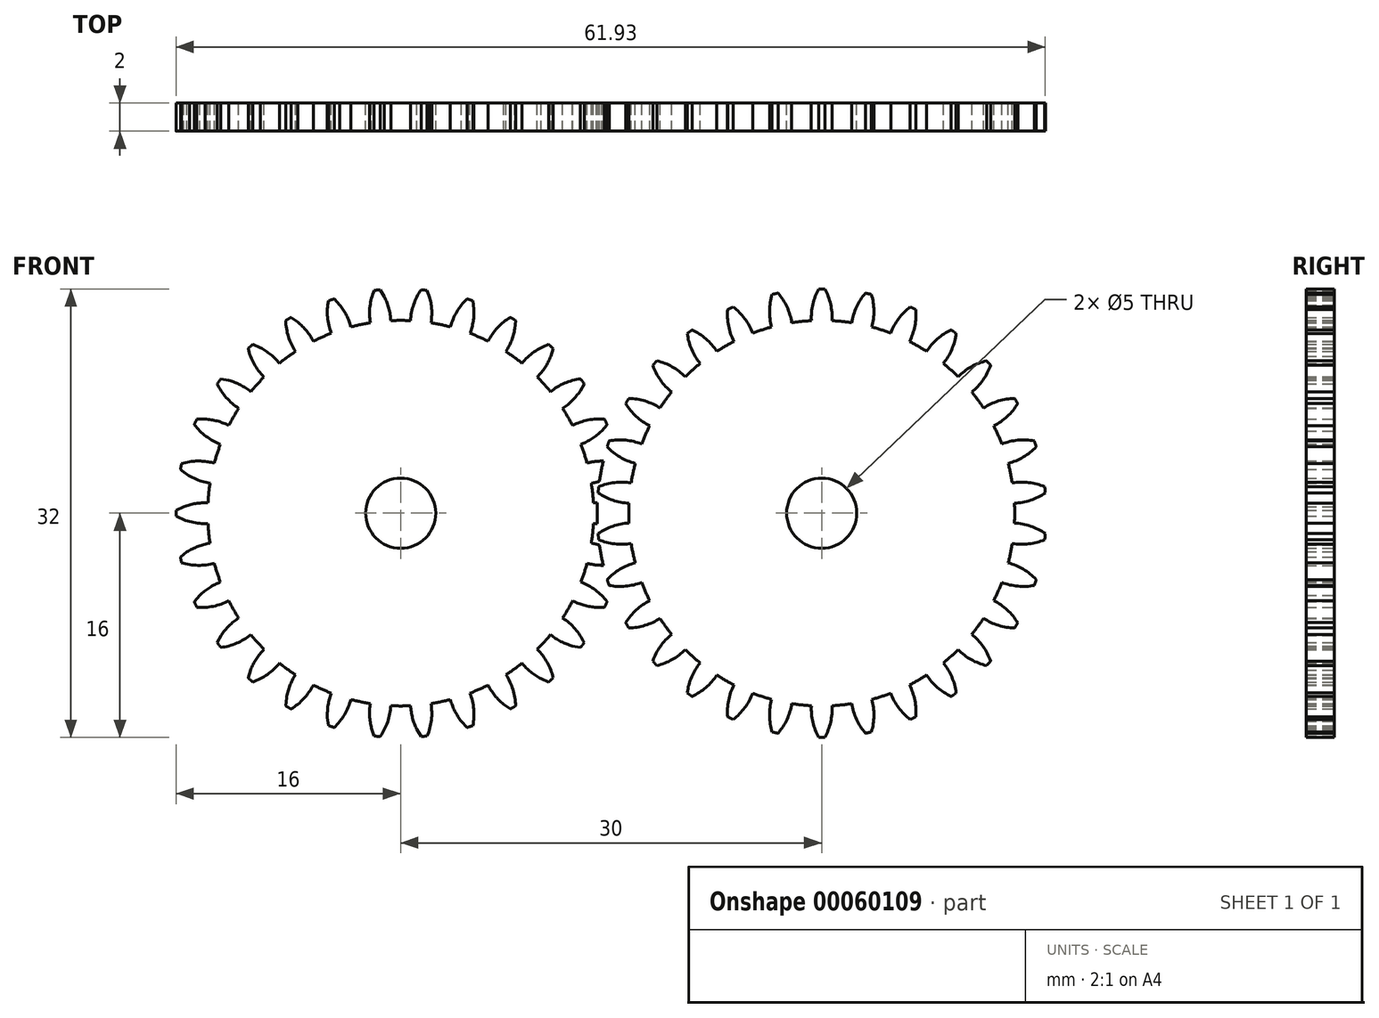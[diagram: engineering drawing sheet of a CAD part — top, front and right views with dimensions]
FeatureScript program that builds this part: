
annotation { "Feature Type Name" : "Feature", "Feature Type Description" : "" }
export const myFeature = defineFeature(function(context is Context, id is Id, definition is map)
    precondition{}
    {
        {
            assignVariable(context, id + "F0", {"name" : "Module", "anyValue" : 1});
        }
        {
            assignVariable(context, id + "F1", {"name" : "CenterDistance", "anyValue" : 30});
        }
        {
            assignVariable(context, id + "F2", {"name" : "Ratio", "anyValue" : 1});
        }
        {
            assignVariable(context, id + "F3", {"name" : "Width", "anyValue" : 2});
        }
        {
            assignVariable(context, id + "F4", {"name" : "TotalTeeth", "anyValue" : (2 * getVariable(context, 'CenterDistance')) / getVariable(context, 'Module')});
        }
        {
            assignVariable(context, id + "F5", {"name" : "TeethQuanity1", "anyValue" : getVariable(context, 'TotalTeeth') / (getVariable(context, 'Ratio') + 1)});
        }
        {
            assignVariable(context, id + "F6", {"name" : "TeethQuanity2", "anyValue" : (getVariable(context, 'Ratio') * getVariable(context, 'TotalTeeth')) / (getVariable(context, 'Ratio') + 1)});
        }
        {
            assignVariable(context, id + "F7", {"name" : "CenterDistance", "anyValue" : (getVariable(context, 'TotalTeeth') * getVariable(context, 'Module')) / 2});
        }
        {
            var Q0;
            Q0=qCreatedBy(makeId("Front.planeOp"),FACE);
            var sketch = newSketch(context, id + "F8", { "sketchPlane" : qUnion([Q0])});
            skCircle(sketch, "E0", {"center": v(-15, 0) * mm, "radius": 13.75 * mm});
            skCircle(sketch, "E1", {"center": v(-15, 0) * mm, "radius": 15 * mm, "construction": true});
            skCircle(sketch, "E2", {"center": v(-15, 0) * mm, "radius": 16 * mm});
            skLineSegment(sketch, "E3", {"start": v(-15, 0) * mm, "end": v(-15, 44.34) * mm, "construction": true});
            skArc(sketch, "E4", {"start": v(-15.7, 13.73) * mm, "mid": v(-15.84, 14.6) * mm, "end": v(-16.16, 15.43) * mm});
            skArc(sketch, "E5.MirrorCS", {"start": v(-14.3, 13.73) * mm, "mid": v(-13.64, 15.79) * mm, "end": v(-12.06, 17.26) * mm});
            skArc(sketch, "E6", {"start": v(-12.06, 17.26) * mm, "mid": v(-15, 17.51) * mm, "end": v(-17.94, 17.26) * mm});
            skLineSegment(sketch, "E7", {"start": v(-15.7, 13.73) * mm, "end": v(-15, 0) * mm, "construction": true});
            skLineSegment(sketch, "E8", {"start": v(-15, 12.34) * mm, "end": v(-15.96, 14.97) * mm, "construction": true});
            skLineSegment(sketch, "E9", {"start": v(-15, 0) * mm, "end": v(-19.76, 45.29) * mm, "construction": true});
            skLineSegment(sketch, "E10", {"start": v(0, 0) * mm, "end": v(-15, 0) * mm, "construction": true});
            skPoint(sketch, "E11.endSnap0", {"position": v(-16.46, 15.93) * mm});
            skArc(sketch, "E12.trimOffspring", {"start": v(-16.46, 15.93) * mm, "mid": v(-17.12, 16.69) * mm, "end": v(-17.94, 17.26) * mm});
            skLineSegment(sketch, "E13", {"start": v(-16.16, 15.43) * mm, "end": v(-16.46, 15.93) * mm});
            skLineSegment(sketch, "E14", {"start": v(-16.16, 15.43) * mm, "end": v(-16.16, 15.43) * mm});
            skCircle(sketch, "E15", {"center": v(-15, 0) * mm, "radius": 14.1 * mm, "construction": true});
            skLineSegment(sketch, "E16", {"start": v(-14.26, 14.08) * mm, "end": v(-15.74, 14.08) * mm, "construction": true});
            skLineSegment(sketch, "E17", {"start": v(-15.74, 14.08) * mm, "end": v(-17.2, 13.92) * mm, "construction": true});
            skCircle(sketch, "E18", {"center": v(-15, 0) * mm, "radius": 2.5 * mm});
            skSolve(sketch);
        }
        {
            var Q0;
            {var subQ0=sQuery(id+"F8.wireOp",EDGE,"E4");var subQ1=sQuery(id+"F8.wireOp",EDGE,"E0");var subQ2=makeQuery(id+"F8.imprint","INTERSECT",VERTEX,{"derivedFrom":[subQ1,subQ0]});Q0=makeQuery(id+"F8.imprint","IMPRINT",FACE,{"disambiguationData":[TD([[makeQuery(id+"F8.imprint","IMPRINT",EDGE,{"disambiguationData":[TD([[subQ2,-1.0]])],"derivedFrom":subQ1}),-1.0]])]});}
            var Q1;
            {var subQ0=sQuery(id+"F8.wireOp",EDGE,"E0");var subQ1=makeQuery(id+"F8.imprint","INTERSECT",VERTEX,{"derivedFrom":[subQ0,sQuery(id+"F8.wireOp",EDGE,"E4")]});Q1=makeQuery(id+"F8.imprint","IMPRINT",FACE,{"disambiguationData":[TD([[makeQuery(id+"F8.imprint","IMPRINT",EDGE,{"disambiguationData":[TD([[subQ1,1.0]])],"derivedFrom":subQ0}),1.0]])]});}
            var Q2;
            Q2=sQuery(id+"F8.wireOp",EDGE,"E2");
            extrude(context, id + "F9", {"entities" : qUnion([Q0, Q1]), "surfaceEntities" : qUnion([Q2]), "endBound" : BoundingType.SYMMETRIC, "depth" : (getVariable(context, 'Width')) * mm});
        }
        {
            var Q0;
            {var subQ0=sQuery(id+"F8.wireOp",EDGE,"E4");var subQ1=sQuery(id+"F8.wireOp",EDGE,"E0");var subQ2=makeQuery(id+"F8.imprint","INTERSECT",VERTEX,{"derivedFrom":[subQ1,subQ0]});Q0=makeQuery(id+"F8.imprint","IMPRINT",FACE,{"disambiguationData":[TD([[makeQuery(id+"F8.imprint","IMPRINT",EDGE,{"disambiguationData":[TD([[subQ2,1.0]])],"derivedFrom":subQ1}),-1.0]])]});}
            extrude(context, id + "F10", {"entities" : qUnion([Q0]), "endBound" : BoundingType.SYMMETRIC, "depth" : (getVariable(context, 'Width')) * mm});
        }
        {
            var Q0;
            Q0=makeQuery(id+"F10.opExtrude","SWEPT_BODY",BODY,{"disambiguationData":[OSD([sQuery(id+"F8.wireOp",EDGE,"E0"),sQuery(id+"F8.wireOp",EDGE,"E2"),sQuery(id+"F8.wireOp",EDGE,"E4"),sQuery(id+"F8.wireOp",EDGE,"E5.MirrorCS")])]});
            var Q1;
            Q1=sQuery(id+"F8.wireOp",EDGE,"E2");
            circularPattern(context, id + "F11", {"operationType" : NewBodyOperationType.REMOVE, "entities" : qUnion([Q0]), "axis" : qUnion([Q1]), "angle" : 360 * degree, "instanceCount" : round(getVariable(context, 'TeethQuanity1')), "equalSpace" : true});
        }
        {
            var Q0;
            Q0=qCreatedBy(makeId("Front.planeOp"),FACE);
            var sketch = newSketch(context, id + "F12", { "sketchPlane" : qUnion([Q0])});
            skCircle(sketch, "E19", {"center": v(15, 0) * mm, "radius": 13.75 * mm});
            skCircle(sketch, "E20", {"center": v(15, 0) * mm, "radius": 15 * mm, "construction": true});
            skCircle(sketch, "E21", {"center": v(15, 0) * mm, "radius": 16 * mm});
            skLineSegment(sketch, "E22", {"start": v(15, 0) * mm, "end": v(21.14, 58.4) * mm, "construction": true});
            skArc(sketch, "E23", {"start": v(15.73, 13.73) * mm, "mid": v(15.57, 15.16) * mm, "end": v(14.93, 16.46) * mm});
            skArc(sketch, "E24.MirrorCS", {"start": v(17.14, 13.58) * mm, "mid": v(17.6, 14.95) * mm, "end": v(18.5, 16.08) * mm});
            skArc(sketch, "E25", {"start": v(18.5, 16.08) * mm, "mid": v(16.72, 16.37) * mm, "end": v(14.93, 16.46) * mm});
            skLineSegment(sketch, "E26", {"start": v(15.73, 13.73) * mm, "end": v(15, 0) * mm, "construction": true});
            skLineSegment(sketch, "E27", {"start": v(16.29, 12.27) * mm, "end": v(15.61, 14.99) * mm, "construction": true});
            skLineSegment(sketch, "E28", {"start": v(15, 0) * mm, "end": v(15, 57.16) * mm, "construction": true});
            skLineSegment(sketch, "E29", {"start": v(0, 0) * mm, "end": v(15, 0) * mm, "construction": true});
            skCircle(sketch, "E30", {"center": v(15, 0) * mm, "radius": 14.1 * mm, "construction": true});
            skLineSegment(sketch, "E31", {"start": v(17.2, 13.92) * mm, "end": v(15.74, 14.08) * mm, "construction": true});
            skLineSegment(sketch, "E32", {"start": v(15.74, 14.08) * mm, "end": v(14.26, 14.08) * mm, "construction": true});
            skCircle(sketch, "E33", {"center": v(15, 0) * mm, "radius": 2.5 * mm});
            skSolve(sketch);
        }
        {
            var Q0;
            {var subQ0=sQuery(id+"F12.wireOp",EDGE,"E23");var subQ1=sQuery(id+"F12.wireOp",EDGE,"E19");var subQ2=makeQuery(id+"F12.imprint","INTERSECT",VERTEX,{"derivedFrom":[subQ1,subQ0]});Q0=makeQuery(id+"F12.imprint","IMPRINT",FACE,{"disambiguationData":[TD([[makeQuery(id+"F12.imprint","IMPRINT",EDGE,{"disambiguationData":[TD([[subQ2,-1.0]])],"derivedFrom":subQ1}),-1.0]])]});}
            var Q1;
            {var subQ0=sQuery(id+"F12.wireOp",EDGE,"E19");var subQ1=makeQuery(id+"F12.imprint","INTERSECT",VERTEX,{"derivedFrom":[subQ0,sQuery(id+"F12.wireOp",EDGE,"E23")]});Q1=makeQuery(id+"F12.imprint","IMPRINT",FACE,{"disambiguationData":[TD([[makeQuery(id+"F12.imprint","IMPRINT",EDGE,{"disambiguationData":[TD([[subQ1,1.0]])],"derivedFrom":subQ0}),1.0]])]});}
            extrude(context, id + "F13", {"entities" : qUnion([Q0, Q1]), "endBound" : BoundingType.SYMMETRIC, "depth" : (getVariable(context, 'Width')) * mm});
        }
        {
            var Q0;
            {var subQ0=sQuery(id+"F12.wireOp",EDGE,"E23");var subQ1=sQuery(id+"F12.wireOp",EDGE,"E19");var subQ2=makeQuery(id+"F12.imprint","INTERSECT",VERTEX,{"derivedFrom":[subQ1,subQ0]});Q0=makeQuery(id+"F12.imprint","IMPRINT",FACE,{"disambiguationData":[TD([[makeQuery(id+"F12.imprint","IMPRINT",EDGE,{"disambiguationData":[TD([[subQ2,1.0]])],"derivedFrom":subQ1}),-1.0]])]});}
            extrude(context, id + "F14", {"entities" : qUnion([Q0]), "endBound" : BoundingType.SYMMETRIC, "depth" : (getVariable(context, 'Width')) * mm});
        }
        {
            var Q0;
            Q0=makeQuery(id+"F14.opExtrude","SWEPT_BODY",BODY,{"disambiguationData":[OSD([sQuery(id+"F12.wireOp",EDGE,"E19"),sQuery(id+"F12.wireOp",EDGE,"E21"),sQuery(id+"F12.wireOp",EDGE,"E23"),sQuery(id+"F12.wireOp",EDGE,"E24.MirrorCS")])]});
            var Q1;
            Q1=sQuery(id+"F12.wireOp",EDGE,"E21");
            circularPattern(context, id + "F15", {"operationType" : NewBodyOperationType.REMOVE, "entities" : qUnion([Q0]), "axis" : qUnion([Q1]), "angle" : 360 * degree, "instanceCount" : round(getVariable(context, 'TeethQuanity2')), "equalSpace" : true});
        }
    });
